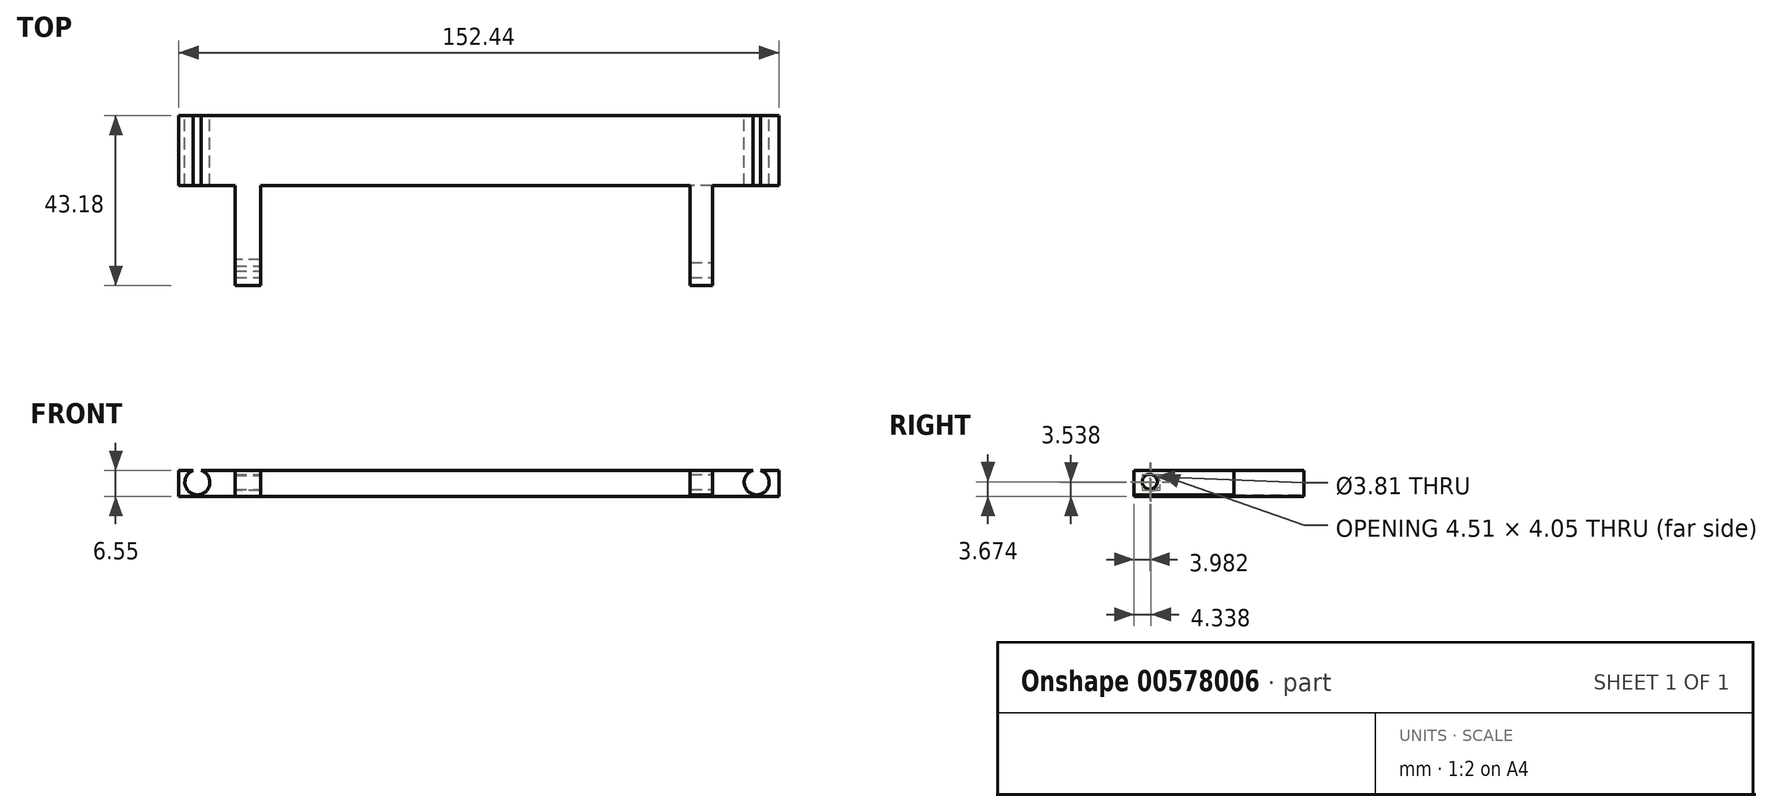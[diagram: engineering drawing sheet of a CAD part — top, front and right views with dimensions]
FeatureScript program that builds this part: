
annotation { "Feature Type Name" : "Feature", "Feature Type Description" : "" }
export const myFeature = defineFeature(function(context is Context, id is Id, definition is map)
    precondition{}
    {
        {
            var Q0;
            Q0=qCreatedBy(makeId("Front.planeOp"),FACE);
            var sketch = newSketch(context, id + "F0", { "sketchPlane" : qUnion([Q0])});
            skLineSegment(sketch, "E0.bottom", {"start": v(-66.7, 50.48) * mm, "end": v(85.74, 50.48) * mm});
            skLineSegment(sketch, "E0.top", {"start": v(-66.7, 43.93) * mm, "end": v(85.74, 43.93) * mm});
            skLineSegment(sketch, "E0.left", {"start": v(-66.7, 50.48) * mm, "end": v(-66.7, 43.93) * mm});
            skLineSegment(sketch, "E0.right", {"start": v(85.74, 50.48) * mm, "end": v(85.74, 43.93) * mm});
            skSolve(sketch);
        }
        {
            var Q0;
            Q0=makeQuery(id+"F0.imprint","IMPRINT",FACE,{"disambiguationData":[TD([[makeQuery(id+"F0.imprint","IMPRINT",EDGE,{"derivedFrom":sQuery(id+"F0.wireOp",EDGE,"E0.bottom")}),-1.0]])]});
            var sketch = newSketch(context, id + "F1", { "sketchPlane" : qUnion([Q0])});
            skPoint(sketch, "E1", {"position": v(-62, 47.47) * mm});
            skSolve(sketch);
        }
        {
            var Q0;
            Q0=makeQuery(id+"F0.imprint","IMPRINT",FACE,{"disambiguationData":[TD([[makeQuery(id+"F0.imprint","IMPRINT",EDGE,{"derivedFrom":sQuery(id+"F0.wireOp",EDGE,"E0.bottom")}),-1.0]])]});
            var sketch = newSketch(context, id + "F2", { "sketchPlane" : qUnion([Q0])});
            skPoint(sketch, "E2", {"position": v(80.1, 47.46) * mm});
            skSolve(sketch);
        }
        {
            var Q0;
            Q0=makeQuery(id+"F0.imprint","IMPRINT",FACE,{"disambiguationData":[TD([[makeQuery(id+"F0.imprint","IMPRINT",EDGE,{"derivedFrom":sQuery(id+"F0.wireOp",EDGE,"E0.bottom")}),-1.0]])]});
            extrude(context, id + "F3", {"entities" : qUnion([Q0]), "depth" : 17.78 * mm, "offsetDistance" : 25.4 * mm});
        }
        {
            var Q0;
            Q0=sQuery(id+"F1.wireOp",VERTEX,"E1");
            var Q1;
            Q1=sQuery(id+"F2.wireOp",VERTEX,"E2");
            var Q2;
            Q2=makeQuery(id+"F3.opExtrude","SWEPT_BODY",BODY,{"disambiguationData":[OSD([sQuery(id+"F0.wireOp",EDGE,"E0.bottom"),sQuery(id+"F0.wireOp",EDGE,"E0.top"),sQuery(id+"F0.wireOp",EDGE,"E0.left"),sQuery(id+"F0.wireOp",EDGE,"E0.right")])]});
            hole(context, id + "F4", {"style" : HoleStyle.SIMPLE, "endStyle" : HoleEndStyle.THROUGH, "oppositeDirection" : true, "holeDiameter" : 6.35 * mm, "isTappedThrough" : true, "tappedDepth" : 12.7 * mm, "tapClearance" : 3, "locations" : qUnion([Q0, Q1]), "scope" : qUnion([Q2])});
        }
        {
            var Q0;
            Q0=makeQuery(id+"F3.opExtrude","CAP_FACE",FACE,{"disambiguationData":[OSD([sQuery(id+"F0.wireOp",EDGE,"E0.bottom"),sQuery(id+"F0.wireOp",EDGE,"E0.top"),sQuery(id+"F0.wireOp",EDGE,"E0.left"),sQuery(id+"F0.wireOp",EDGE,"E0.right")])],"isStart":false});
            var sketch = newSketch(context, id + "F5", { "sketchPlane" : qUnion([Q0])});
            skLineSegment(sketch, "E3", {"start": v(-52.44, 50.48) * mm, "end": v(-52.44, 43.93) * mm});
            skLineSegment(sketch, "E4", {"start": v(-52.44, 43.93) * mm, "end": v(-45.94, 43.93) * mm});
            skLineSegment(sketch, "E5", {"start": v(-45.94, 43.93) * mm, "end": v(-45.94, 50.48) * mm});
            skLineSegment(sketch, "E6", {"start": v(-45.94, 50.48) * mm, "end": v(-52.44, 50.48) * mm});
            skSolve(sketch);
        }
        {
            var Q0;
            {var subQ11=sQuery(id+"F5.wireOp",EDGE,"E5");Q0=makeQuery(id+"F5.imprint","IMPRINT",FACE,{"disambiguationData":[TD([[makeQuery(id+"F5.imprint","IMPRINT",EDGE,{"derivedFrom":subQ11}),-1.0]])]});}
            var sketch = newSketch(context, id + "F6", { "sketchPlane" : qUnion([Q0])});
            skLineSegment(sketch, "E7", {"start": v(68.86, 50.7) * mm, "end": v(68.86, 44.3) * mm});
            skLineSegment(sketch, "E8", {"start": v(68.86, 44.3) * mm, "end": v(63.17, 44.3) * mm});
            skLineSegment(sketch, "E9", {"start": v(63.17, 44.3) * mm, "end": v(63.17, 50.7) * mm});
            skSolve(sketch);
        }
        {
            var Q0;
            {var subQ0=sQuery(id+"F6.wireOp",EDGE,"E8");Q0=makeQuery(id+"F6.imprint","IMPRINT",FACE,{"disambiguationData":[TD([[makeQuery(id+"F6.imprint","IMPRINT",EDGE,{"derivedFrom":subQ0}),-1.0]])]});}
            extrude(context, id + "F7", {"entities" : qUnion([Q0]), "operationType" : NewBodyOperationType.ADD, "depth" : 25.4 * mm, "offsetDistance" : 25.4 * mm});
        }
        {
            var Q0;
            Q0=makeQuery(id+"F5.imprint","IMPRINT",FACE,{"disambiguationData":[TD([[makeQuery(id+"F5.imprint","IMPRINT",EDGE,{"derivedFrom":sQuery(id+"F5.wireOp",EDGE,"E3")}),1.0]])]});
            extrude(context, id + "F8", {"entities" : qUnion([Q0]), "operationType" : NewBodyOperationType.ADD, "depth" : 25.4 * mm, "offsetDistance" : 25.4 * mm});
        }
        {
            var Q0;
            Q0=makeQuery(id+"F8.opExtrude","SWEPT_FACE",FACE,{"disambiguationData":[OSD([sQuery(id+"F5.wireOp",EDGE,"E3")])]});
            var sketch = newSketch(context, id + "F9", { "sketchPlane" : qUnion([Q0])});
            skPoint(sketch, "E10", {"position": v(38.49, 47.33) * mm});
            skSolve(sketch);
        }
        {
            var Q0;
            Q0=sQuery(id+"F9.wireOp",VERTEX,"E10");
            var Q1;
            Q1=makeQuery(id+"F3.opExtrude","SWEPT_BODY",BODY,{"disambiguationData":[OSD([sQuery(id+"F0.wireOp",EDGE,"E0.bottom"),sQuery(id+"F0.wireOp",EDGE,"E0.top"),sQuery(id+"F0.wireOp",EDGE,"E0.left"),sQuery(id+"F0.wireOp",EDGE,"E0.right")])]});
            hole(context, id + "F10", {"style" : HoleStyle.SIMPLE, "endStyle" : HoleEndStyle.BLIND, "holeDiameter" : 3.8 * mm, "holeDepth" : 12.7 * mm, "isTappedThrough" : true, "tappedDepth" : 12.7 * mm, "tapClearance" : 3, "locations" : qUnion([Q0]), "scope" : qUnion([Q1])});
        }
        {
            var Q0;
            Q0=makeQuery(id+"F7.opExtrude","SWEPT_FACE",FACE,{"disambiguationData":[OSD([sQuery(id+"F6.wireOp",EDGE,"E7")])]});
            var sketch = newSketch(context, id + "F11", { "sketchPlane" : qUnion([Q0])});
            skPoint(sketch, "E11", {"position": v(-39.2, 47.6) * mm});
            skSolve(sketch);
        }
        {
            var Q0;
            Q0=sQuery(id+"F11.wireOp",VERTEX,"E11");
            var Q1;
            Q1=makeQuery(id+"F3.opExtrude","SWEPT_BODY",BODY,{"disambiguationData":[OSD([sQuery(id+"F0.wireOp",EDGE,"E0.bottom"),sQuery(id+"F0.wireOp",EDGE,"E0.top"),sQuery(id+"F0.wireOp",EDGE,"E0.left"),sQuery(id+"F0.wireOp",EDGE,"E0.right")])]});
            hole(context, id + "F12", {"style" : HoleStyle.SIMPLE, "endStyle" : HoleEndStyle.THROUGH, "holeDiameter" : 3.8 * mm, "isTappedThrough" : true, "tappedDepth" : 12.7 * mm, "tapClearance" : 3, "locations" : qUnion([Q0]), "scope" : qUnion([Q1])});
        }
    });
